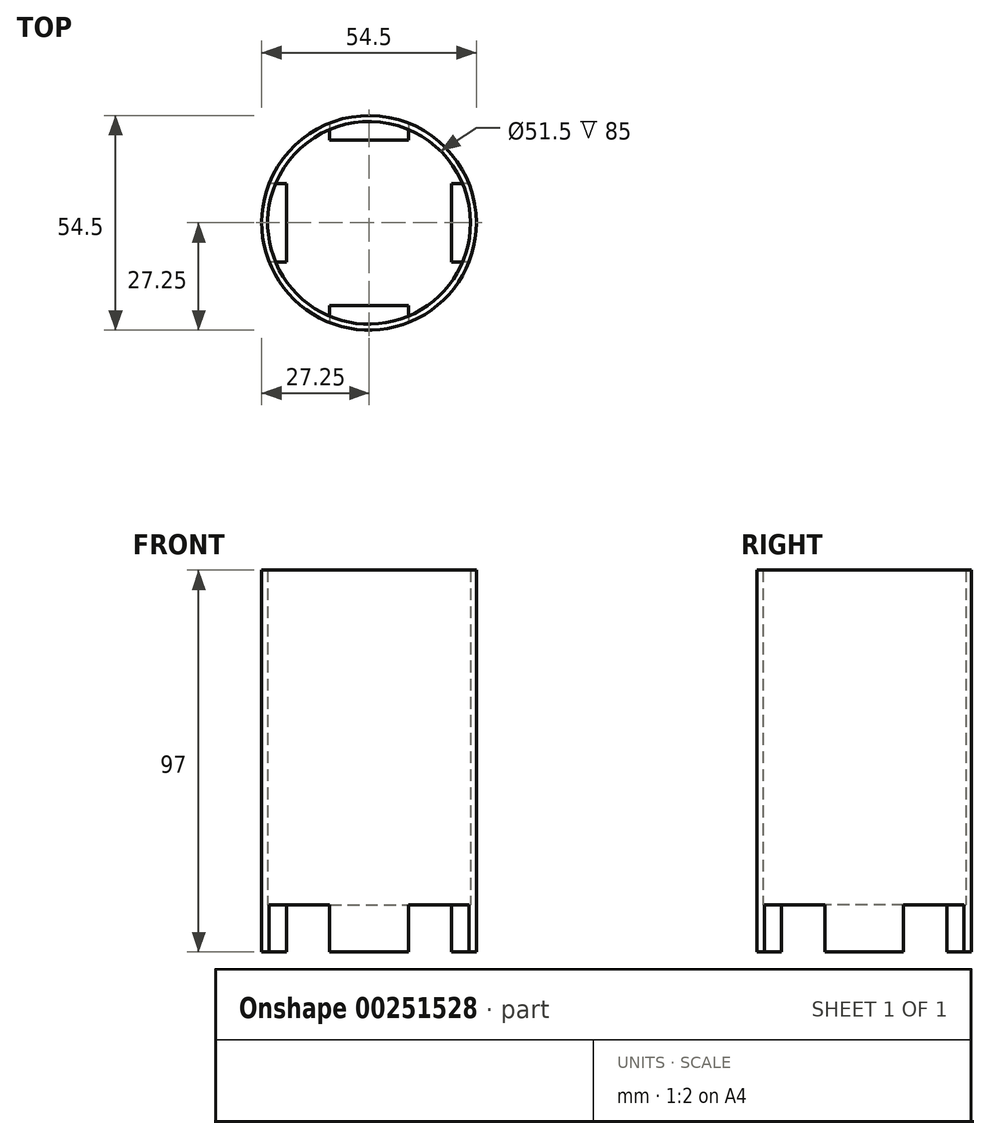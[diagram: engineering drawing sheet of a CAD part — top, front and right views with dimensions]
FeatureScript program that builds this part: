
annotation { "Feature Type Name" : "Feature", "Feature Type Description" : "" }
export const myFeature = defineFeature(function(context is Context, id is Id, definition is map)
    precondition{}
    {
        {
            var Q0;
            Q0=qCreatedBy(makeId("Top.planeOp"),FACE);
            var sketch = newSketch(context, id + "F0", { "sketchPlane" : qUnion([Q0])});
            skCircle(sketch, "E0", {"center": v(0, 0) * mm, "radius": 27.25 * mm});
            skCircle(sketch, "E1", {"center": v(0, 0) * mm, "radius": 25.75 * mm});
            skSolve(sketch);
        }
        {
            var Q0;
            Q0 = qSketchRegion(id + "F0", true);
            extrude(context, id + "F1", {"entities" : qUnion([Q0]), "depth" : 85 * mm});
        }
        {
            var Q0;
            Q0=qCreatedBy(makeId("Top.planeOp"),FACE);
            var sketch = newSketch(context, id + "F2", { "sketchPlane" : qUnion([Q0])});
            skLineSegment(sketch, "E2.bottom", {"start": v(-10, 38.5) * mm, "end": v(10, 38.5) * mm});
            skLineSegment(sketch, "E2.top", {"start": v(-10, -38.5) * mm, "end": v(10, -38.5) * mm});
            skLineSegment(sketch, "E2.left", {"start": v(-10, 38.5) * mm, "end": v(-10, -38.5) * mm});
            skLineSegment(sketch, "E2.right", {"start": v(10, 38.5) * mm, "end": v(10, -38.5) * mm});
            skPoint(sketch, "E2.middle", {"position": v(0, 0) * mm});
            skLineSegment(sketch, "E3.bottom", {"start": v(35.6, 10) * mm, "end": v(-35.6, 10) * mm});
            skLineSegment(sketch, "E3.top", {"start": v(35.6, -10) * mm, "end": v(-35.6, -10) * mm});
            skLineSegment(sketch, "E3.left", {"start": v(35.6, 10) * mm, "end": v(35.6, -10) * mm});
            skLineSegment(sketch, "E3.right", {"start": v(-35.6, 10) * mm, "end": v(-35.6, -10) * mm});
            skLineSegment(sketch, "E4.bottom", {"start": v(-21, 21) * mm, "end": v(21, 21) * mm});
            skLineSegment(sketch, "E4.top", {"start": v(-21, -21) * mm, "end": v(21, -21) * mm});
            skLineSegment(sketch, "E4.left", {"start": v(-21, 21) * mm, "end": v(-21, -21) * mm});
            skLineSegment(sketch, "E4.right", {"start": v(21, 21) * mm, "end": v(21, -21) * mm});
            skSolve(sketch);
        }
        {
            var Q0;
            {var subQ0=sQuery(id+"F2.wireOp",EDGE,"E2.top");Q0=makeQuery(id+"F2.imprint","IMPRINT",FACE,{"disambiguationData":[TD([[makeQuery(id+"F2.imprint","IMPRINT",EDGE,{"derivedFrom":subQ0}),1.0]])]});}
            var Q1;
            {var subQ0=sQuery(id+"F2.wireOp",EDGE,"E3.right");Q1=makeQuery(id+"F2.imprint","IMPRINT",FACE,{"disambiguationData":[TD([[makeQuery(id+"F2.imprint","IMPRINT",EDGE,{"derivedFrom":subQ0}),1.0]])]});}
            var Q2;
            {var subQ0=sQuery(id+"F2.wireOp",EDGE,"E2.bottom");Q2=makeQuery(id+"F2.imprint","IMPRINT",FACE,{"disambiguationData":[TD([[makeQuery(id+"F2.imprint","IMPRINT",EDGE,{"derivedFrom":subQ0}),-1.0]])]});}
            var Q3;
            {var subQ0=sQuery(id+"F2.wireOp",EDGE,"E3.left");Q3=makeQuery(id+"F2.imprint","IMPRINT",FACE,{"disambiguationData":[TD([[makeQuery(id+"F2.imprint","IMPRINT",EDGE,{"derivedFrom":subQ0}),-1.0]])]});}
            extrude(context, id + "F3", {"entities" : qUnion([Q0, Q1, Q2, Q3]), "operationType" : NewBodyOperationType.ADD, "oppositeDirection" : true, "depth" : 12 * mm});
        }
        {
            var Q0;
            {var subQ0=sQuery(id+"F2.wireOp",EDGE,"E3.top");var subQ1=sQuery(id+"F2.wireOp",EDGE,"E3.bottom");var subQ2=sQuery(id+"F2.wireOp",EDGE,"E2.right");var subQ3=sQuery(id+"F2.wireOp",EDGE,"E2.left");Q0=makeQuery(id+"F3.boolean.opBoolean","MERGE",FACE,{"derivedFrom":[makeQuery(id+"F1.opExtrude","CAP_FACE",FACE,{"disambiguationData":[OSD([sQuery(id+"F0.wireOp",EDGE,"E0"),sQuery(id+"F0.wireOp",EDGE,"E1")])],"isStart":true}),makeQuery(id+"F3.opExtrude","CAP_FACE",FACE,{"disambiguationData":[OSD([sQuery(id+"F2.wireOp",EDGE,"E2.bottom"),subQ3,subQ2,sQuery(id+"F2.wireOp",EDGE,"E4.bottom")])],"isStart":true}),makeQuery(id+"F3.opExtrude","CAP_FACE",FACE,{"disambiguationData":[OSD([sQuery(id+"F2.wireOp",EDGE,"E2.top"),subQ3,subQ2,sQuery(id+"F2.wireOp",EDGE,"E4.top")])],"isStart":true}),makeQuery(id+"F3.opExtrude","CAP_FACE",FACE,{"disambiguationData":[OSD([subQ1,subQ0,sQuery(id+"F2.wireOp",EDGE,"E3.left"),sQuery(id+"F2.wireOp",EDGE,"E4.right")])],"isStart":true}),makeQuery(id+"F3.opExtrude","CAP_FACE",FACE,{"disambiguationData":[OSD([subQ1,subQ0,sQuery(id+"F2.wireOp",EDGE,"E3.right"),sQuery(id+"F2.wireOp",EDGE,"E4.left")])],"isStart":true})]});}
            var sketch = newSketch(context, id + "F4", { "sketchPlane" : qUnion([Q0])});
            skCircle(sketch, "E5", {"center": v(0, 0) * mm, "radius": 27.25 * mm});
            skSolve(sketch);
        }
        {
            var Q0;
            Q0 = qSketchRegion(id + "F4", true);
            extrude(context, id + "F5", {"entities" : qUnion([Q0]), "operationType" : NewBodyOperationType.INTERSECT, "endBound" : BoundingType.SYMMETRIC, "depth" : 200 * mm});
        }
    });
